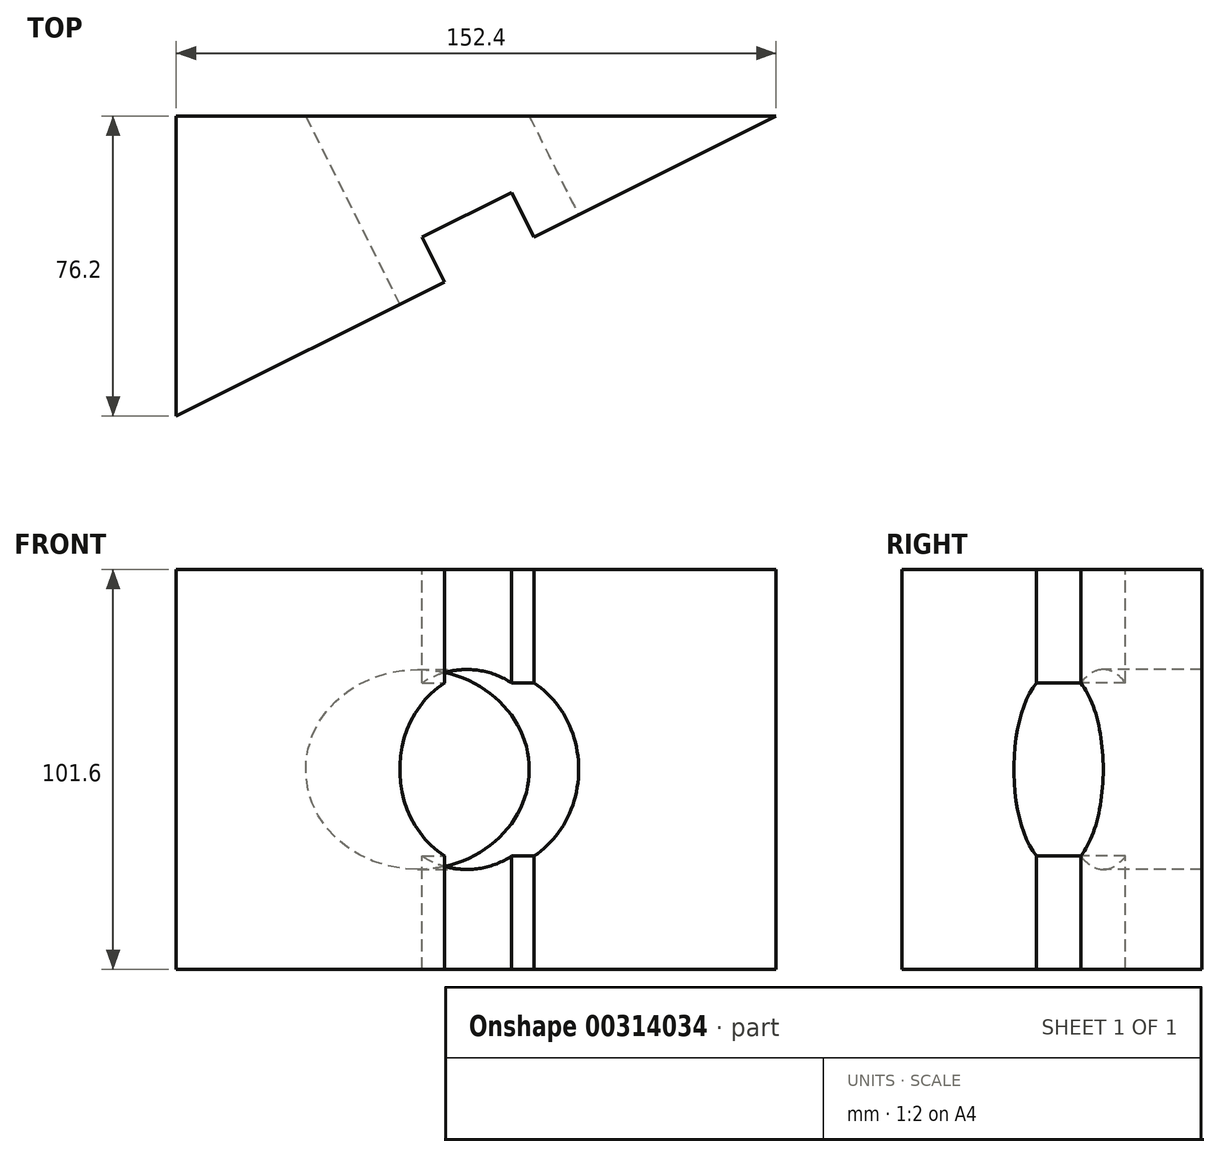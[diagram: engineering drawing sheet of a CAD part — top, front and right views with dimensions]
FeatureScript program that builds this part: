
annotation { "Feature Type Name" : "Feature", "Feature Type Description" : "" }
export const myFeature = defineFeature(function(context is Context, id is Id, definition is map)
    precondition{}
    {
        {
            var Q0;
            Q0=qCreatedBy(makeId("Top.planeOp"),FACE);
            var sketch = newSketch(context, id + "F0", { "sketchPlane" : qUnion([Q0])});
            skLineSegment(sketch, "E0.bottom", {"start": v(0, 0) * mm, "end": v(152.4, 0) * mm});
            skLineSegment(sketch, "E0.top", {"start": v(0, -76.2) * mm, "end": v(152.4, -76.2) * mm});
            skLineSegment(sketch, "E0.left", {"start": v(0, 0) * mm, "end": v(0, -76.2) * mm});
            skLineSegment(sketch, "E0.right", {"start": v(152.4, 0) * mm, "end": v(152.4, -76.2) * mm});
            skLineSegment(sketch, "E1", {"start": v(0, -76.2) * mm, "end": v(152.4, 0) * mm});
            skSolve(sketch);
        }
        {
            var Q0;
            Q0=makeQuery(id+"F0.imprint","IMPRINT",FACE,{"disambiguationData":[TD([[makeQuery(id+"F0.imprint","IMPRINT",EDGE,{"derivedFrom":sQuery(id+"F0.wireOp",EDGE,"E0.bottom")}),-1.0]])]});
            extrude(context, id + "F1", {"entities" : qUnion([Q0]), "depth" : 101.6 * mm});
        }
        {
            var Q0;
            Q0=makeQuery(id+"F1.opExtrude","SWEPT_FACE",FACE,{"disambiguationData":[OSD([sQuery(id+"F0.wireOp",EDGE,"E1")])]});
            var sketch = newSketch(context, id + "F2", { "sketchPlane" : qUnion([Q0])});
            skLineSegment(sketch, "E2.bottom", {"start": v(67.52, 0) * mm, "end": v(42.12, 0) * mm});
            skLineSegment(sketch, "E2.top", {"start": v(67.52, 101.6) * mm, "end": v(42.12, 101.6) * mm});
            skLineSegment(sketch, "E2.left", {"start": v(67.52, 0) * mm, "end": v(67.52, 101.6) * mm});
            skLineSegment(sketch, "E2.right", {"start": v(42.12, 0) * mm, "end": v(42.12, 101.6) * mm});
            skPoint(sketch, "E2.middle", {"position": v(54.82, 50.8) * mm});
            skSolve(sketch);
        }
        {
            var Q0;
            Q0=makeQuery(id+"F2.imprint","IMPRINT",FACE,{"disambiguationData":[TD([[makeQuery(id+"F2.imprint","IMPRINT",EDGE,{"derivedFrom":sQuery(id+"F2.wireOp",EDGE,"E2.bottom")}),1.0]])]});
            extrude(context, id + "F3", {"entities" : qUnion([Q0]), "operationType" : NewBodyOperationType.REMOVE, "oppositeDirection" : true, "depth" : 12.7 * mm});
        }
        {
            var Q0;
            {var subQ0=sQuery(id+"F0.wireOp",EDGE,"E1");var subQ1=sQuery(id+"F0.wireOp",EDGE,"E0.left");Q0=makeQuery(id+"F3.boolean.opBoolean","SPLIT",FACE,{"disambiguationData":[TD([makeQuery(id+"F1.opExtrude","SWEPT_FACE",FACE,{"disambiguationData":[OSD([subQ1])]})])],"derivedFrom":makeQuery(id+"F1.opExtrude","SWEPT_FACE",FACE,{"disambiguationData":[OSD([subQ0])]})});}
            var sketch = newSketch(context, id + "F4", { "sketchPlane" : qUnion([Q0])});
            skCircle(sketch, "E3", {"center": v(54.82, 50.8) * mm, "radius": 25.4 * mm});
            skSolve(sketch);
        }
        {
            var Q0;
            {var subQ0=sQuery(id+"F4.wireOp",EDGE,"E3");var subQ1=makeQuery(id+"F3.boolean.opBoolean","COPY",EDGE,{"derivedFrom":makeQuery(id+"F3.opExtrude","CAP_EDGE",EDGE,{"disambiguationData":[OSD([sQuery(id+"F2.wireOp",EDGE,"E2.right")])],"isStart":true})});var subQ2=makeQuery(id+"F4.imprint","INTERSECT",VERTEX,{"disambiguationData":[OD(0.0)],"derivedFrom":[subQ1,subQ0]});Q0=makeQuery(id+"F4.imprint","IMPRINT",FACE,{"disambiguationData":[TD([[makeQuery(id+"F4.imprint","IMPRINT",EDGE,{"disambiguationData":[TD([[subQ2,-1.0]])],"derivedFrom":subQ0}),1.0]])]});}
            var Q1;
            {var subQ0=sQuery(id+"F4.wireOp",EDGE,"E3");var subQ1=makeQuery(id+"F3.boolean.opBoolean","COPY",EDGE,{"derivedFrom":makeQuery(id+"F3.opExtrude","CAP_EDGE",EDGE,{"disambiguationData":[OSD([sQuery(id+"F2.wireOp",EDGE,"E2.right")])],"isStart":true})});var subQ2=makeQuery(id+"F4.imprint","INTERSECT",VERTEX,{"disambiguationData":[OD(0.0)],"derivedFrom":[subQ1,subQ0]});Q1=makeQuery(id+"F4.imprint","IMPRINT",FACE,{"disambiguationData":[TD([[makeQuery(id+"F4.imprint","IMPRINT",EDGE,{"disambiguationData":[TD([[subQ2,1.0]])],"derivedFrom":subQ0}),1.0]])]});}
            extrude(context, id + "F5", {"entities" : qUnion([Q0, Q1]), "operationType" : NewBodyOperationType.REMOVE, "endBound" : BoundingType.THROUGH_ALL, "oppositeDirection" : true, "depth" : 25.4 * mm});
        }
    });
